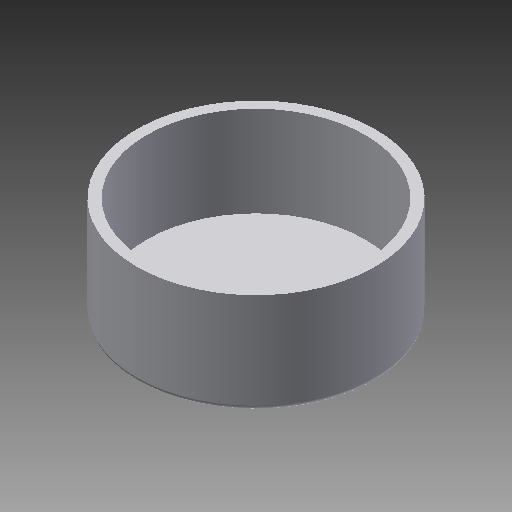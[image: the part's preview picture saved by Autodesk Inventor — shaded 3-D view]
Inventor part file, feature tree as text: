
AUTODESK INVENTOR PART (.ipt)
format: ipt  version: 2017 (Build 210142000, 142)  size: 95,744 bytes
history: native  units: in
note: dims shown in document units (in); Inventor stores cm internally (conversion verified against a paired STEP export)
features: fillet x1, other x1, imported_body x1
ambient origin geometry x8: Origin, YZ Plane, XZ Plane, XY Plane, X Axis, Y Axis, Z Axis, Center Point
bodies: Body1 (feature_tree)
feature tree (3):
  fillet  "Fillet1"  [1 undecoded]
  other  "light reflector.ipt1"
  imported_body  "Base1"
note: 1 required parameter value undecoded (feature->parameter linkage not recoverable at this tier; creation-order binding heuristic only, values carry confidence <= 0.55)
